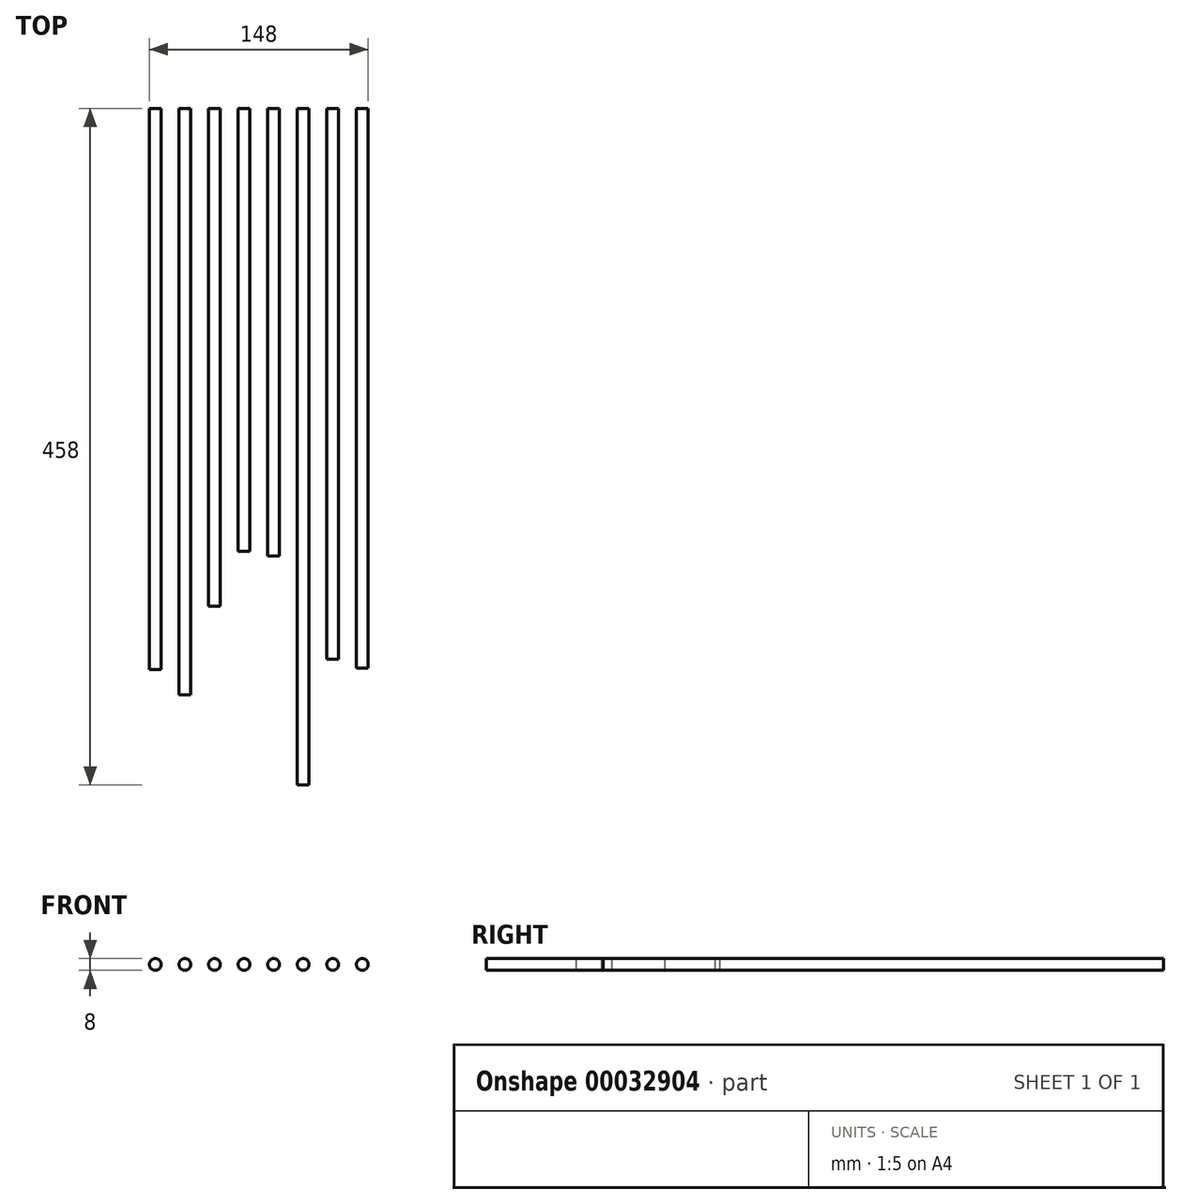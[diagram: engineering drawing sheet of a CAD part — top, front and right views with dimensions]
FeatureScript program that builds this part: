
annotation { "Feature Type Name" : "Feature", "Feature Type Description" : "" }
export const myFeature = defineFeature(function(context is Context, id is Id, definition is map)
    precondition{}
    {
        {
            var Q0;
            Q0=qCreatedBy(makeId("Front.planeOp"),FACE);
            var sketch = newSketch(context, id + "F0", { "sketchPlane" : qUnion([Q0])});
            skCircle(sketch, "E0", {"center": v(0, 0) * mm, "radius": 4 * mm});
            skCircle(sketch, "E1.1.0.0", {"center": v(20, 0) * mm, "radius": 4 * mm});
            skCircle(sketch, "E1.2.0.0", {"center": v(40, 0) * mm, "radius": 4 * mm});
            skCircle(sketch, "E1.3.0.0", {"center": v(60, 0) * mm, "radius": 4 * mm});
            skCircle(sketch, "E1.4.0.0", {"center": v(80, 0) * mm, "radius": 4 * mm});
            skCircle(sketch, "E1.5.0.0", {"center": v(100, 0) * mm, "radius": 4 * mm});
            skCircle(sketch, "E1.6.0.0", {"center": v(120, 0) * mm, "radius": 4 * mm});
            skCircle(sketch, "E1.7.0.0", {"center": v(140, 0) * mm, "radius": 4 * mm});
            skLineSegment(sketch, "E1.direction1", {"start": v(0, 0) * mm, "end": v(20, 0) * mm, "construction": true});
            skSolve(sketch);
        }
        {
            var Q0;
            Q0=makeQuery(id+"F0.imprint","IMPRINT",FACE,{"disambiguationData":[TD([[makeQuery(id+"F0.imprint","IMPRINT",EDGE,{"derivedFrom":sQuery(id+"F0.wireOp",EDGE,"E0")}),1.0]])]});
            extrude(context, id + "F1", {"entities" : qUnion([Q0]), "depth" : 380 * mm});
        }
        {
            var Q0;
            Q0=makeQuery(id+"F0.imprint","IMPRINT",FACE,{"disambiguationData":[TD([[makeQuery(id+"F0.imprint","IMPRINT",EDGE,{"derivedFrom":sQuery(id+"F0.wireOp",EDGE,"E1.1.0.0")}),1.0]])]});
            extrude(context, id + "F2", {"entities" : qUnion([Q0]), "depth" : 397 * mm});
        }
        {
            var Q0;
            Q0=makeQuery(id+"F0.imprint","IMPRINT",FACE,{"disambiguationData":[TD([[makeQuery(id+"F0.imprint","IMPRINT",EDGE,{"derivedFrom":sQuery(id+"F0.wireOp",EDGE,"E1.2.0.0")}),1.0]])]});
            extrude(context, id + "F3", {"entities" : qUnion([Q0]), "depth" : 337 * mm});
        }
        {
            var Q0;
            Q0=makeQuery(id+"F0.imprint","IMPRINT",FACE,{"disambiguationData":[TD([[makeQuery(id+"F0.imprint","IMPRINT",EDGE,{"derivedFrom":sQuery(id+"F0.wireOp",EDGE,"E1.3.0.0")}),1.0]])]});
            extrude(context, id + "F4", {"entities" : qUnion([Q0]), "depth" : 300 * mm});
        }
        {
            var Q0;
            Q0=makeQuery(id+"F0.imprint","IMPRINT",FACE,{"disambiguationData":[TD([[makeQuery(id+"F0.imprint","IMPRINT",EDGE,{"derivedFrom":sQuery(id+"F0.wireOp",EDGE,"E1.4.0.0")}),1.0]])]});
            extrude(context, id + "F5", {"entities" : qUnion([Q0]), "depth" : 303 * mm});
        }
        {
            var Q0;
            Q0=makeQuery(id+"F0.imprint","IMPRINT",FACE,{"disambiguationData":[TD([[makeQuery(id+"F0.imprint","IMPRINT",EDGE,{"derivedFrom":sQuery(id+"F0.wireOp",EDGE,"E1.5.0.0")}),1.0]])]});
            extrude(context, id + "F6", {"entities" : qUnion([Q0]), "depth" : 458 * mm});
        }
        {
            var Q0;
            Q0=makeQuery(id+"F0.imprint","IMPRINT",FACE,{"disambiguationData":[TD([[makeQuery(id+"F0.imprint","IMPRINT",EDGE,{"derivedFrom":sQuery(id+"F0.wireOp",EDGE,"E1.6.0.0")}),1.0]])]});
            extrude(context, id + "F7", {"entities" : qUnion([Q0]), "depth" : 373 * mm});
        }
        {
            var Q0;
            Q0=makeQuery(id+"F0.imprint","IMPRINT",FACE,{"disambiguationData":[TD([[makeQuery(id+"F0.imprint","IMPRINT",EDGE,{"derivedFrom":sQuery(id+"F0.wireOp",EDGE,"E1.7.0.0")}),1.0]])]});
            extrude(context, id + "F8", {"entities" : qUnion([Q0]), "depth" : 379 * mm});
        }
    });
